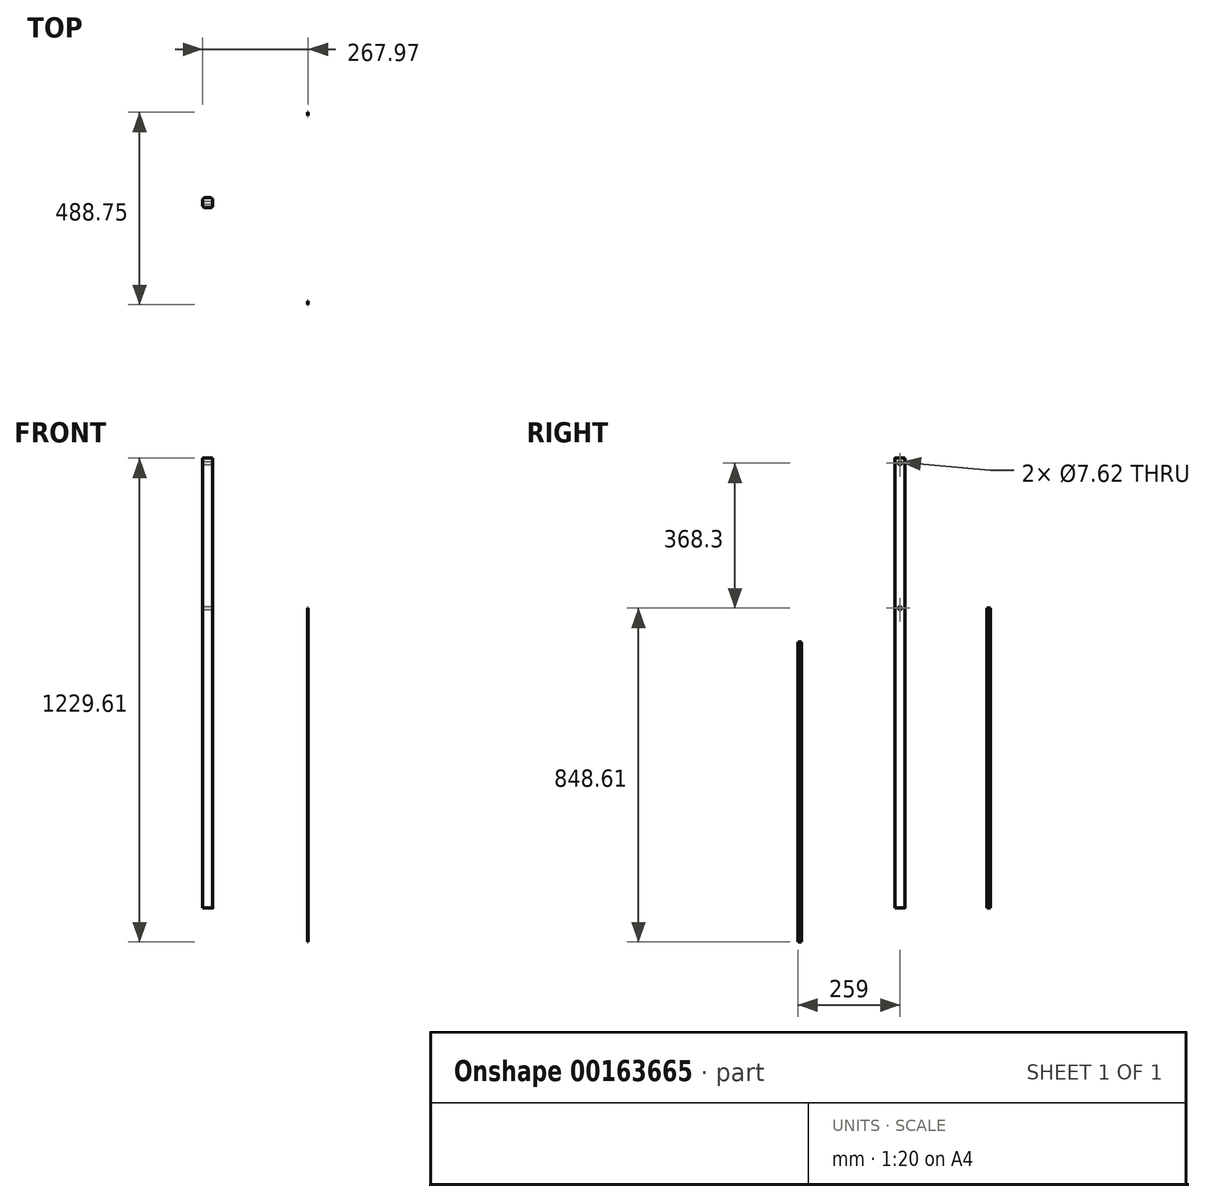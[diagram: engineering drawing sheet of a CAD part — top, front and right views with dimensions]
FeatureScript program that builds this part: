
annotation { "Feature Type Name" : "Feature", "Feature Type Description" : "" }
export const myFeature = defineFeature(function(context is Context, id is Id, definition is map)
    precondition{}
    {
        {
            var Q0;
            Q0=qCreatedBy(makeId("Top.planeOp"),FACE);
            var sketch = newSketch(context, id + "F0", { "sketchPlane" : qUnion([Q0])});
            skLineSegment(sketch, "E0.bottom", {"start": v(6.35, 12.7) * mm, "end": v(-6.35, 12.7) * mm});
            skLineSegment(sketch, "E0.top", {"start": v(6.35, -12.7) * mm, "end": v(-6.35, -12.7) * mm});
            skLineSegment(sketch, "E0.left", {"start": v(12.7, 6.35) * mm, "end": v(12.7, -6.35) * mm});
            skLineSegment(sketch, "E0.right", {"start": v(-12.7, 6.35) * mm, "end": v(-12.7, -6.35) * mm});
            skPoint(sketch, "E0.middle", {"position": v(0, 0) * mm});
            skPoint(sketch, "E1.visualSharp", {"position": v(-12.7, 12.7) * mm});
            skArc(sketch, "E1.filletArc", {"start": v(-6.35, 12.7) * mm, "mid": v(-10.84, 10.84) * mm, "end": v(-12.7, 6.35) * mm});
            skPoint(sketch, "E2.visualSharp", {"position": v(-12.7, -12.7) * mm});
            skArc(sketch, "E2.filletArc", {"start": v(-12.7, -6.35) * mm, "mid": v(-10.84, -10.84) * mm, "end": v(-6.35, -12.7) * mm});
            skPoint(sketch, "E3.visualSharp", {"position": v(12.7, -12.7) * mm});
            skArc(sketch, "E3.filletArc", {"start": v(6.35, -12.7) * mm, "mid": v(10.84, -10.84) * mm, "end": v(12.7, -6.35) * mm});
            skPoint(sketch, "E4.visualSharp", {"position": v(12.7, 12.7) * mm});
            skArc(sketch, "E4.filletArc", {"start": v(12.7, 6.35) * mm, "mid": v(10.84, 10.84) * mm, "end": v(6.35, 12.7) * mm});
            skSolve(sketch);
        }
        {
            var Q0;
            Q0=qSketchRegion(id+"F0",true);
            extrude(context, id + "F1", {"entities" : qUnion([Q0]), "depth" : 1143 * mm});
        }
        {
            var Q0;
            Q0=qCreatedBy(makeId("Right.planeOp"),FACE);
            var sketch = newSketch(context, id + "F2", { "sketchPlane" : qUnion([Q0])});
            skLineSegment(sketch, "E5.bottom", {"start": v(-259, 675.39) * mm, "end": v(-250.53, 675.39) * mm});
            skLineSegment(sketch, "E5.top", {"start": v(-259, -86.61) * mm, "end": v(-250.53, -86.61) * mm});
            skLineSegment(sketch, "E5.left", {"start": v(-259, 675.39) * mm, "end": v(-259, -86.61) * mm});
            skLineSegment(sketch, "E5.right", {"start": v(-250.53, 675.39) * mm, "end": v(-250.53, -86.61) * mm});
            skSolve(sketch);
        }
        {
            var Q0;
            Q0=makeQuery(id+"F2.imprint","IMPRINT",FACE,{"disambiguationData":[TD([[makeQuery(id+"F2.imprint","IMPRINT",EDGE,{"derivedFrom":sQuery(id+"F2.wireOp",EDGE,"E5.bottom")}),-1.0]])]});
            extrude(context, id + "F3", {"entities" : qUnion([Q0]), "depth" : 1.27 * mm});
        }
        {
            var Q0;
            Q0=qCreatedBy(makeId("Right.planeOp"),FACE);
            var sketch = newSketch(context, id + "F4", { "sketchPlane" : qUnion([Q0])});
            skLineSegment(sketch, "E6.bottom", {"start": v(221.29, 762) * mm, "end": v(229.75, 762) * mm});
            skLineSegment(sketch, "E6.top", {"start": v(221.29, 0) * mm, "end": v(229.75, 0) * mm});
            skLineSegment(sketch, "E6.left", {"start": v(221.29, 762) * mm, "end": v(221.29, 0) * mm});
            skLineSegment(sketch, "E6.right", {"start": v(229.75, 762) * mm, "end": v(229.75, 0) * mm});
            skSolve(sketch);
        }
        {
            var Q0;
            Q0=makeQuery(id+"F4.imprint","IMPRINT",FACE,{"disambiguationData":[TD([[makeQuery(id+"F4.imprint","IMPRINT",EDGE,{"derivedFrom":sQuery(id+"F4.wireOp",EDGE,"E6.bottom")}),-1.0]])]});
            var Q1;
            Q1=sQuery(id+"F4.wireOp",EDGE,"E6.right");
            var Q2;
            Q2=sQuery(id+"F4.wireOp",EDGE,"E6.left");
            var Q3;
            Q3=sQuery(id+"F4.wireOp",EDGE,"E6.top");
            var Q4;
            Q4=sQuery(id+"F4.wireOp",EDGE,"E6.bottom");
            extrude(context, id + "F5", {"entities" : qUnion([Q0]), "surfaceEntities" : qUnion([Q1, Q2, Q3, Q4]), "depth" : 1.27 * mm});
        }
        {
            var Q0;
            Q0=makeQuery(id+"F3.opExtrude","SWEPT_BODY",BODY,{"disambiguationData":[OSD([sQuery(id+"F2.wireOp",EDGE,"E5.bottom"),sQuery(id+"F2.wireOp",EDGE,"E5.top"),sQuery(id+"F2.wireOp",EDGE,"E5.left"),sQuery(id+"F2.wireOp",EDGE,"E5.right")])]});
            var Q1;
            Q1=makeQuery(id+"F5.opExtrude","SWEPT_BODY",BODY,{"disambiguationData":[OSD([sQuery(id+"F4.wireOp",EDGE,"E6.bottom"),sQuery(id+"F4.wireOp",EDGE,"E6.top"),sQuery(id+"F4.wireOp",EDGE,"E6.left"),sQuery(id+"F4.wireOp",EDGE,"E6.right")])]});
            transform(context, id + "F6", {"entities" : qUnion([Q0, Q1]), "transformType" : TransformType.TRANSLATION_3D, "dx" : 254 * mm, "dy" : 0 * mm, "dz" : 0 * mm, "makeCopy" : false});
        }
        {
            var Q0;
            Q0=makeQuery(id+"F1.opExtrude","SWEPT_FACE",FACE,{"disambiguationData":[OSD([sQuery(id+"F0.wireOp",EDGE,"E0.left")])]});
            var sketch = newSketch(context, id + "F7", { "sketchPlane" : qUnion([Q0])});
            skPoint(sketch, "E7.endSnap0", {"position": v(0, 1143) * mm});
            skCircle(sketch, "E8", {"center": v(0, 1130.3) * mm, "radius": 3.81 * mm});
            skCircle(sketch, "E9", {"center": v(0, 762) * mm, "radius": 3.81 * mm});
            skSolve(sketch);
        }
        {
            var Q0;
            Q0 = qSketchRegion(id + "F7", true);
            extrude(context, id + "F8", {"entities" : qUnion([Q0]), "operationType" : NewBodyOperationType.REMOVE, "oppositeDirection" : true, "depth" : 25.4 * mm});
        }
        {
            var Q0;
            Q0 = qSketchRegion(id + "F7", true);
            extrude(context, id + "F9", {"entities" : qUnion([Q0]), "operationType" : NewBodyOperationType.REMOVE, "oppositeDirection" : true, "depth" : 25.4 * mm});
        }
    });
